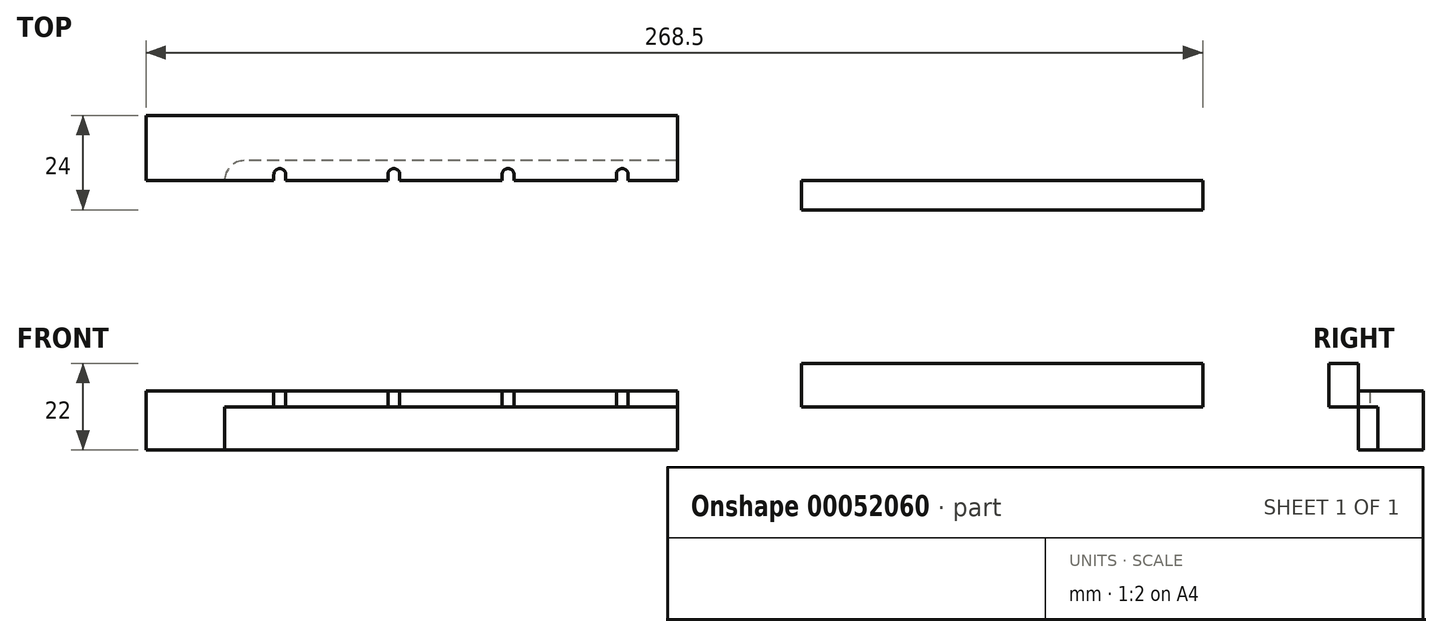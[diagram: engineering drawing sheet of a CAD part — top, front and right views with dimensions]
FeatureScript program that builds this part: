
annotation { "Feature Type Name" : "Feature", "Feature Type Description" : "" }
export const myFeature = defineFeature(function(context is Context, id is Id, definition is map)
    precondition{}
    {
        {
            var Q0;
            Q0=qCreatedBy(makeId("Top.planeOp"),FACE);
            var sketch = newSketch(context, id + "F0", { "sketchPlane" : qUnion([Q0])});
            skLineSegment(sketch, "E0", {"start": v(67.5, 0) * mm, "end": v(67.5, 16.5) * mm});
            skLineSegment(sketch, "E1", {"start": v(67.5, 16.5) * mm, "end": v(-67.5, 16.5) * mm});
            skLineSegment(sketch, "E2", {"start": v(-67.5, 16.5) * mm, "end": v(-67.5, 0) * mm});
            skLineSegment(sketch, "E3", {"start": v(-43.24, 1.5) * mm, "end": v(84.67, 1.5) * mm, "construction": true});
            skArc(sketch, "E4", {"start": v(55, 1.5) * mm, "mid": v(53.5, 3) * mm, "end": v(52, 1.5) * mm});
            skArc(sketch, "E5", {"start": v(26, 1.5) * mm, "mid": v(24.5, 3) * mm, "end": v(23, 1.5) * mm});
            skArc(sketch, "E6", {"start": v(-3, 1.5) * mm, "mid": v(-4.5, 3) * mm, "end": v(-6, 1.5) * mm});
            skArc(sketch, "E7", {"start": v(-32, 1.5) * mm, "mid": v(-33.5, 3) * mm, "end": v(-35, 1.5) * mm});
            skLineSegment(sketch, "E8", {"start": v(52, 1.5) * mm, "end": v(52, 0) * mm});
            skLineSegment(sketch, "E9", {"start": v(55, 1.5) * mm, "end": v(55, 0) * mm});
            skLineSegment(sketch, "E10", {"start": v(26, 1.5) * mm, "end": v(26, 0) * mm});
            skLineSegment(sketch, "E11", {"start": v(23, 1.5) * mm, "end": v(23, 0) * mm});
            skLineSegment(sketch, "E12", {"start": v(-6, 1.5) * mm, "end": v(-6, 0) * mm});
            skLineSegment(sketch, "E13", {"start": v(-3, 1.5) * mm, "end": v(-3, 0) * mm});
            skLineSegment(sketch, "E14", {"start": v(-35, 1.5) * mm, "end": v(-35, 0) * mm});
            skLineSegment(sketch, "E15", {"start": v(-32, 1.5) * mm, "end": v(-32, 0) * mm});
            skLineSegment(sketch, "E16.trimOffspring", {"start": v(-32, 0) * mm, "end": v(-6, 0) * mm});
            skLineSegment(sketch, "E17", {"start": v(-35, 0) * mm, "end": v(-67.5, 0) * mm});
            skLineSegment(sketch, "E18.trimOffspring", {"start": v(-3, 0) * mm, "end": v(23, 0) * mm});
            skLineSegment(sketch, "E19.trimOffspring", {"start": v(26, 0) * mm, "end": v(52, 0) * mm});
            skLineSegment(sketch, "E20.trimOffspring", {"start": v(55, 0) * mm, "end": v(67.5, 0) * mm});
            skSolve(sketch);
        }
        {
            var Q0;
            Q0=makeQuery(id+"F0.imprint","IMPRINT",FACE,{"disambiguationData":[TD([[makeQuery(id+"F0.imprint","IMPRINT",EDGE,{"derivedFrom":sQuery(id+"F0.wireOp",EDGE,"E0")}),1.0]])]});
            extrude(context, id + "F1", {"entities" : qUnion([Q0]), "depth" : 4 * mm});
        }
        {
            var Q0;
            Q0=makeQuery(id+"F1.opExtrude","CAP_FACE",FACE,{"disambiguationData":[OSD([sQuery(id+"F0.wireOp",EDGE,"E0"),sQuery(id+"F0.wireOp",EDGE,"E1"),sQuery(id+"F0.wireOp",EDGE,"E2"),sQuery(id+"F0.wireOp",EDGE,"E4"),sQuery(id+"F0.wireOp",EDGE,"E5"),sQuery(id+"F0.wireOp",EDGE,"E6"),sQuery(id+"F0.wireOp",EDGE,"E7"),sQuery(id+"F0.wireOp",EDGE,"E8"),sQuery(id+"F0.wireOp",EDGE,"E9"),sQuery(id+"F0.wireOp",EDGE,"E10"),sQuery(id+"F0.wireOp",EDGE,"E11"),sQuery(id+"F0.wireOp",EDGE,"E12"),sQuery(id+"F0.wireOp",EDGE,"E13"),sQuery(id+"F0.wireOp",EDGE,"E14"),sQuery(id+"F0.wireOp",EDGE,"E15"),sQuery(id+"F0.wireOp",EDGE,"E16.trimOffspring"),sQuery(id+"F0.wireOp",EDGE,"E17"),sQuery(id+"F0.wireOp",EDGE,"E18.trimOffspring"),sQuery(id+"F0.wireOp",EDGE,"E19.trimOffspring"),sQuery(id+"F0.wireOp",EDGE,"E20.trimOffspring")])],"isStart":true});
            var sketch = newSketch(context, id + "F2", { "sketchPlane" : qUnion([Q0])});
            skPoint(sketch, "E21", {"position": v(67.5, 0) * mm});
            skPoint(sketch, "E22", {"position": v(67.5, -16.5) * mm});
            skPoint(sketch, "E23", {"position": v(-67.5, -16.5) * mm});
            skPoint(sketch, "E24", {"position": v(-67.5, 0) * mm});
            skLineSegment(sketch, "E25.bottom", {"start": v(67.5, 0) * mm, "end": v(-67.5, 0) * mm});
            skLineSegment(sketch, "E25.top", {"start": v(67.5, -16.5) * mm, "end": v(-67.5, -16.5) * mm});
            skLineSegment(sketch, "E25.left", {"start": v(67.5, 0) * mm, "end": v(67.5, -16.5) * mm});
            skLineSegment(sketch, "E25.right", {"start": v(-67.5, 0) * mm, "end": v(-67.5, -16.5) * mm});
            skLineSegment(sketch, "E26.0", {"start": v(67.5, -5) * mm, "end": v(-47.5, -5) * mm});
            skLineSegment(sketch, "E27.0", {"start": v(-47.5, 0) * mm, "end": v(-47.5, -5) * mm});
            skSolve(sketch);
        }
        {
            var Q0;
            {var subQ0=sQuery(id+"F2.wireOp",EDGE,"E25.top");Q0=makeQuery(id+"F2.imprint","IMPRINT",FACE,{"disambiguationData":[TD([[makeQuery(id+"F2.imprint","IMPRINT",EDGE,{"derivedFrom":subQ0}),-1.0]])]});}
            extrude(context, id + "F3", {"entities" : qUnion([Q0]), "operationType" : NewBodyOperationType.ADD, "depth" : 11 * mm});
        }
        {
            var Q0;
            Q0=qCreatedBy(makeId("Right.planeOp"),FACE);
            cPlane(context, id + "F4", {"entities" : qUnion([Q0]), "cplaneType" : CPlaneType.OFFSET, "offset" : 150 * mm, "width" : 150 * mm, "height" : 150 * mm});
        }
        {
            var Q0;
            Q0=qCreatedBy(id+"F4.planeOp",FACE);
            var sketch = newSketch(context, id + "F5", { "sketchPlane" : qUnion([Q0])});
            skLineSegment(sketch, "E28", {"start": v(0, 0) * mm, "end": v(-7.5, 0) * mm});
            skLineSegment(sketch, "E29", {"start": v(-7.5, 0) * mm, "end": v(-7.5, 11) * mm});
            skLineSegment(sketch, "E30", {"start": v(-7.5, 11) * mm, "end": v(0, 11) * mm});
            skLineSegment(sketch, "E31", {"start": v(0, 11) * mm, "end": v(0, 0) * mm});
            skSolve(sketch);
        }
        {
            var Q0;
            Q0=makeQuery(id+"F5.imprint","IMPRINT",FACE,{"disambiguationData":[TD([[makeQuery(id+"F5.imprint","IMPRINT",EDGE,{"derivedFrom":sQuery(id+"F5.wireOp",EDGE,"E28")}),-1.0]])]});
            extrude(context, id + "F6", {"entities" : qUnion([Q0]), "endBound" : BoundingType.SYMMETRIC, "depth" : 102 * mm});
        }
        {
            var Q0;
            Q0=makeQuery(id+"F3.opExtrude","SWEPT_EDGE",EDGE,{"disambiguationData":[OSD([sQuery(id+"F2.wireOp",EDGE,"E26.0"),sQuery(id+"F2.wireOp",EDGE,"E27.0")])]});
            fillet(context, id + "F7", {"entities" : qUnion([Q0]), "radius" : 5 * mm, "tangentPropagation" : true, "allowEdgeOverflow" : false});
        }
    });
